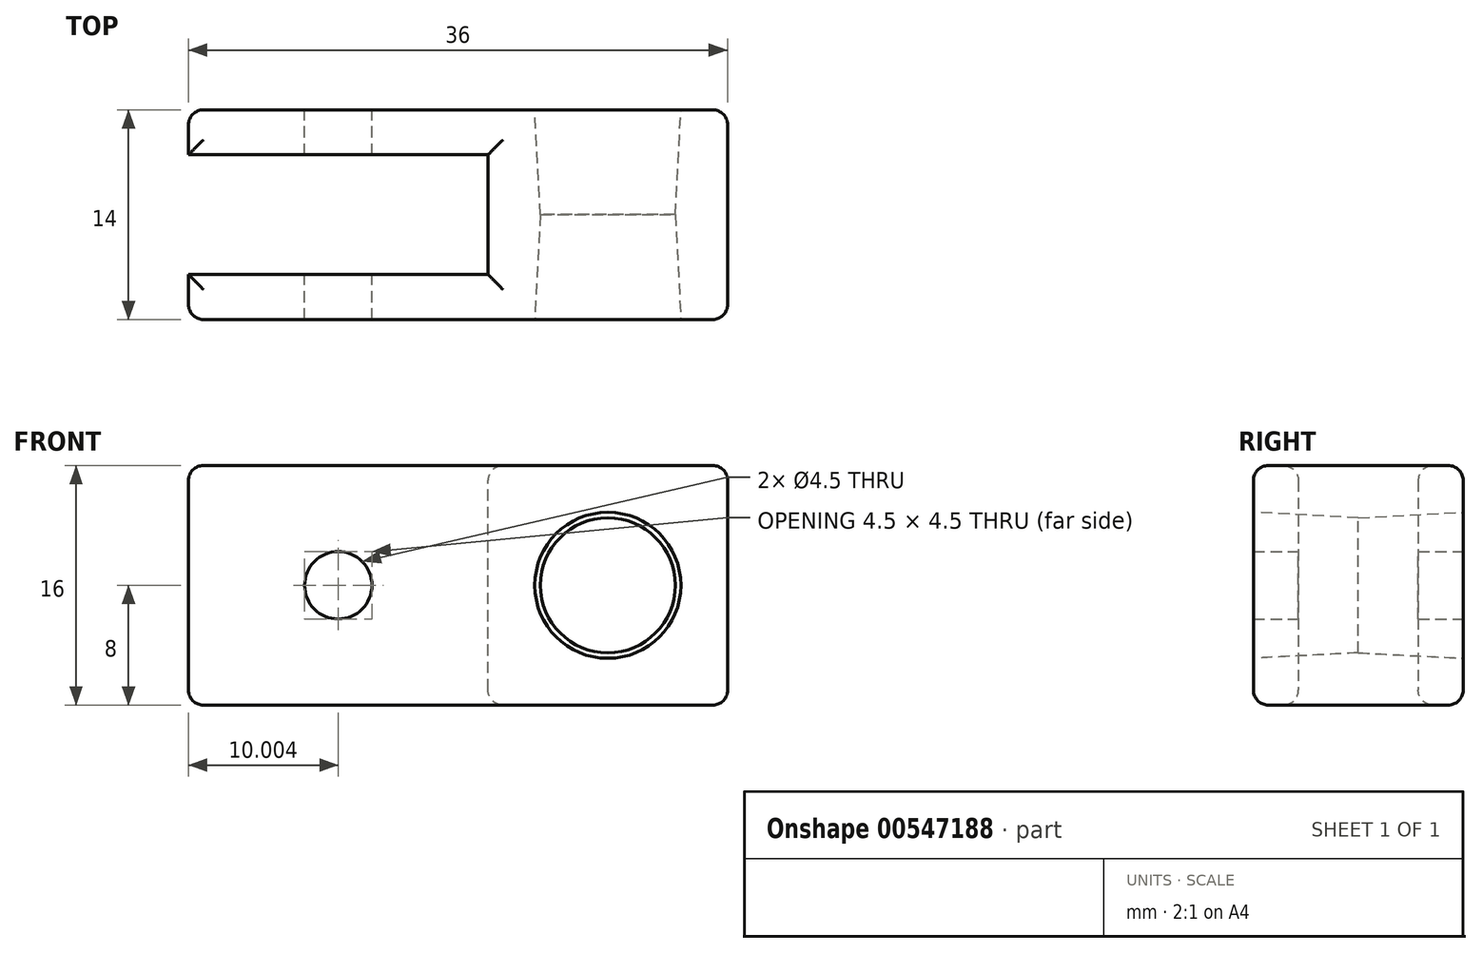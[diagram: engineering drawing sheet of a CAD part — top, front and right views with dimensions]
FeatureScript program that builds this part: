
annotation { "Feature Type Name" : "Feature", "Feature Type Description" : "" }
export const myFeature = defineFeature(function(context is Context, id is Id, definition is map)
    precondition{}
    {
        {
            var Q0;
            Q0=qCreatedBy(makeId("Top.planeOp"),FACE);
            var sketch = newSketch(context, id + "F0", { "sketchPlane" : qUnion([Q0])});
            skLineSegment(sketch, "E0.bottom", {"start": v(-9.79, 4.22) * mm, "end": v(26.21, 4.22) * mm});
            skLineSegment(sketch, "E0.top", {"start": v(-9.79, -9.78) * mm, "end": v(26.21, -9.78) * mm});
            skLineSegment(sketch, "E0.left", {"start": v(-9.79, 4.22) * mm, "end": v(-9.79, -9.78) * mm});
            skLineSegment(sketch, "E0.right", {"start": v(26.21, 4.22) * mm, "end": v(26.21, -9.78) * mm});
            skSolve(sketch);
        }
        {
            var Q0;
            Q0 = qSketchRegion(id + "F0", true);
            extrude(context, id + "F1", {"entities" : qUnion([Q0]), "depth" : 16 * mm, "offsetDistance" : 25 * mm});
        }
        {
            var Q0;
            Q0=makeQuery(id+"F1.opExtrude","CAP_FACE",FACE,{"disambiguationData":[OSD([sQuery(id+"F0.wireOp",EDGE,"E0.bottom"),sQuery(id+"F0.wireOp",EDGE,"E0.top"),sQuery(id+"F0.wireOp",EDGE,"E0.left"),sQuery(id+"F0.wireOp",EDGE,"E0.right")])],"isStart":false});
            var sketch = newSketch(context, id + "F2", { "sketchPlane" : qUnion([Q0])});
            skLineSegment(sketch, "E1.bottom", {"start": v(-40.73, 1.22) * mm, "end": v(10.21, 1.22) * mm});
            skLineSegment(sketch, "E1.top", {"start": v(-40.73, -6.78) * mm, "end": v(10.21, -6.78) * mm});
            skLineSegment(sketch, "E1.left", {"start": v(-40.73, 1.22) * mm, "end": v(-40.73, -6.78) * mm});
            skLineSegment(sketch, "E1.right", {"start": v(10.21, 1.22) * mm, "end": v(10.21, -6.78) * mm});
            skSolve(sketch);
        }
        {
            var Q0;
            {var subQ0=sQuery(id+"F2.wireOp",EDGE,"E1.right");Q0=makeQuery(id+"F2.imprint","IMPRINT",FACE,{"disambiguationData":[TD([[makeQuery(id+"F2.imprint","IMPRINT",EDGE,{"derivedFrom":subQ0}),-1.0]])]});}
            var Q1;
            {var subQ0=sQuery(id+"F2.wireOp",EDGE,"E1.left");Q1=makeQuery(id+"F2.imprint","IMPRINT",FACE,{"disambiguationData":[TD([[makeQuery(id+"F2.imprint","IMPRINT",EDGE,{"derivedFrom":subQ0}),1.0]])]});}
            extrude(context, id + "F3", {"entities" : qUnion([Q0, Q1]), "operationType" : NewBodyOperationType.REMOVE, "endBound" : BoundingType.SYMMETRIC, "oppositeDirection" : true, "depth" : 58.6 * mm, "offsetDistance" : 25 * mm});
        }
        {
            var Q0;
            Q0=makeQuery(id+"F1.opExtrude","SWEPT_FACE",FACE,{"disambiguationData":[OSD([sQuery(id+"F0.wireOp",EDGE,"E0.bottom")])]});
            var sketch = newSketch(context, id + "F4", { "sketchPlane" : qUnion([Q0])});
            skLineSegment(sketch, "E2.0.0", {"start": v(-26.21, 0) * mm, "end": v(9.79, 0) * mm, "construction": true});
            skLineSegment(sketch, "E2.0.1", {"start": v(9.79, 0) * mm, "end": v(9.79, 16) * mm, "construction": true});
            skLineSegment(sketch, "E2.0.2", {"start": v(9.79, 16) * mm, "end": v(-26.21, 16) * mm, "construction": true});
            skLineSegment(sketch, "E2.0.3", {"start": v(-26.21, 16) * mm, "end": v(-26.21, 0) * mm, "construction": true});
            skLineSegment(sketch, "E3.0", {"start": v(-10.21, 0) * mm, "end": v(-10.21, 16) * mm, "construction": true});
            skCircle(sketch, "E4", {"center": v(-18.21, 8) * mm, "radius": 4.88 * mm});
            skCircle(sketch, "E5", {"center": v(-0.21, 8) * mm, "radius": 2.25 * mm});
            skSolve(sketch);
        }
        {
            var Q0;
            Q0=makeQuery(id+"F4.imprint","IMPRINT",FACE,{"disambiguationData":[TD([[makeQuery(id+"F4.imprint","IMPRINT",EDGE,{"derivedFrom":sQuery(id+"F4.wireOp",EDGE,"E4")}),1.0]])]});
            extrude(context, id + "F5", {"entities" : qUnion([Q0]), "operationType" : NewBodyOperationType.REMOVE, "oppositeDirection" : true, "depth" : 11 * mm, "offsetDistance" : 25 * mm, "hasDraft" : true, "draftAngle" : 3 * degree, "draftPullDirection" : true});
        }
        {
            var Q0;
            Q0=makeQuery(id+"F1.opExtrude","SWEPT_FACE",FACE,{"disambiguationData":[OSD([sQuery(id+"F0.wireOp",EDGE,"E0.top")])]});
            var sketch = newSketch(context, id + "F6", { "sketchPlane" : qUnion([Q0])});
            skCircle(sketch, "E6", {"center": v(18.21, 8) * mm, "radius": 4.88 * mm});
            skSolve(sketch);
        }
        {
            var Q0;
            Q0 = qSketchRegion(id + "F6", true);
            extrude(context, id + "F7", {"entities" : qUnion([Q0]), "operationType" : NewBodyOperationType.REMOVE, "oppositeDirection" : true, "depth" : 11 * mm, "offsetDistance" : 25 * mm, "hasDraft" : true, "draftAngle" : 3 * degree, "draftPullDirection" : true});
        }
        {
            var Q0;
            Q0=makeQuery(id+"F1.opExtrude","SWEPT_FACE",FACE,{"disambiguationData":[OSD([sQuery(id+"F0.wireOp",EDGE,"E0.right")])]});
            var Q1;
            Q1=makeQuery(id+"F1.opExtrude","CAP_FACE",FACE,{"disambiguationData":[OSD([sQuery(id+"F0.wireOp",EDGE,"E0.bottom"),sQuery(id+"F0.wireOp",EDGE,"E0.top"),sQuery(id+"F0.wireOp",EDGE,"E0.left"),sQuery(id+"F0.wireOp",EDGE,"E0.right")])],"isStart":false});
            var Q2;
            Q2=makeQuery(id+"F1.opExtrude","CAP_FACE",FACE,{"disambiguationData":[OSD([sQuery(id+"F0.wireOp",EDGE,"E0.bottom"),sQuery(id+"F0.wireOp",EDGE,"E0.top"),sQuery(id+"F0.wireOp",EDGE,"E0.left"),sQuery(id+"F0.wireOp",EDGE,"E0.right")])],"isStart":true});
            var Q3;
            Q3=makeQuery(id+"F1.opExtrude","SWEPT_EDGE",EDGE,{"disambiguationData":[OSD([sQuery(id+"F0.wireOp",EDGE,"E0.bottom"),sQuery(id+"F0.wireOp",EDGE,"E0.left")])]});
            var Q4;
            Q4=makeQuery(id+"F1.opExtrude","SWEPT_EDGE",EDGE,{"disambiguationData":[OSD([sQuery(id+"F0.wireOp",EDGE,"E0.top"),sQuery(id+"F0.wireOp",EDGE,"E0.left")])]});
            fillet(context, id + "F8", {"entities" : qUnion([Q0, Q1, Q2, Q3, Q4]), "radius" : 1 * mm, "tangentPropagation" : true, "allowEdgeOverflow" : false});
        }
        {
            var Q0;
            Q0=makeQuery(id+"F4.imprint","IMPRINT",FACE,{"disambiguationData":[TD([[makeQuery(id+"F4.imprint","IMPRINT",EDGE,{"derivedFrom":sQuery(id+"F4.wireOp",EDGE,"E5")}),1.0]])]});
            extrude(context, id + "F9", {"entities" : qUnion([Q0]), "operationType" : NewBodyOperationType.REMOVE, "endBound" : BoundingType.SYMMETRIC, "oppositeDirection" : true, "depth" : 32 * mm, "offsetDistance" : 25 * mm});
        }
    });
